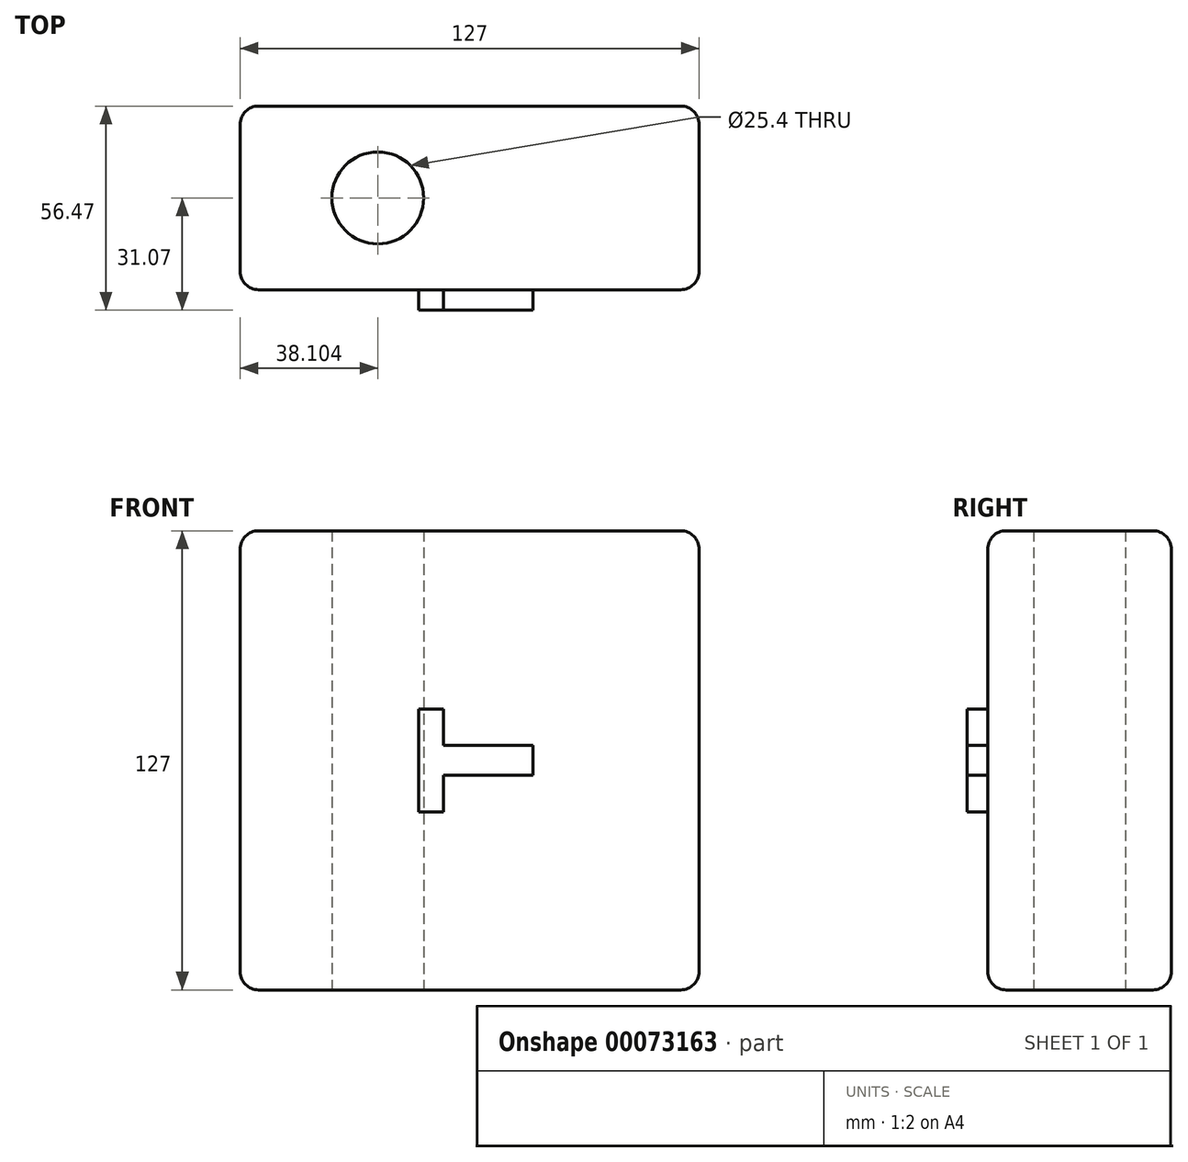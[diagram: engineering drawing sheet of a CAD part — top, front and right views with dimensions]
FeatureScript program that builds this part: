
annotation { "Feature Type Name" : "Feature", "Feature Type Description" : "" }
export const myFeature = defineFeature(function(context is Context, id is Id, definition is map)
    precondition{}
    {
        {
            var Q0;
            Q0=qCreatedBy(makeId("Front.planeOp"),FACE);
            var sketch = newSketch(context, id + "F0", { "sketchPlane" : qUnion([Q0])});
            skLineSegment(sketch, "E0.bottom", {"start": v(-63.03, 57.85) * mm, "end": v(63.97, 57.85) * mm});
            skLineSegment(sketch, "E0.top", {"start": v(-63.03, -69.15) * mm, "end": v(63.97, -69.15) * mm});
            skLineSegment(sketch, "E0.left", {"start": v(-63.03, 57.85) * mm, "end": v(-63.03, -69.15) * mm});
            skLineSegment(sketch, "E0.right", {"start": v(63.97, 57.85) * mm, "end": v(63.97, -69.15) * mm});
            skSolve(sketch);
        }
        {
            var Q0;
            Q0=makeQuery(id+"F0.imprint","IMPRINT",FACE,{"disambiguationData":[TD([[makeQuery(id+"F0.imprint","IMPRINT",EDGE,{"derivedFrom":sQuery(id+"F0.wireOp",EDGE,"E0.bottom")}),-1.0]])]});
            extrude(context, id + "F1", {"entities" : qUnion([Q0]), "depth" : 50.8 * mm});
        }
        {
            var Q0;
            Q0=makeQuery(id+"F1.opExtrude","CAP_EDGE",EDGE,{"disambiguationData":[OSD([sQuery(id+"F0.wireOp",EDGE,"E0.top")])],"isStart":false});
            var Q1;
            Q1=makeQuery(id+"F1.opExtrude","CAP_EDGE",EDGE,{"disambiguationData":[OSD([sQuery(id+"F0.wireOp",EDGE,"E0.top")])],"isStart":true});
            var Q2;
            Q2=makeQuery(id+"F1.opExtrude","CAP_EDGE",EDGE,{"disambiguationData":[OSD([sQuery(id+"F0.wireOp",EDGE,"E0.bottom")])],"isStart":true});
            var Q3;
            Q3=makeQuery(id+"F1.opExtrude","CAP_EDGE",EDGE,{"disambiguationData":[OSD([sQuery(id+"F0.wireOp",EDGE,"E0.bottom")])],"isStart":false});
            var Q4;
            Q4=makeQuery(id+"F1.opExtrude","CAP_EDGE",EDGE,{"disambiguationData":[OSD([sQuery(id+"F0.wireOp",EDGE,"E0.left")])],"isStart":false});
            var Q5;
            Q5=makeQuery(id+"F1.opExtrude","CAP_EDGE",EDGE,{"disambiguationData":[OSD([sQuery(id+"F0.wireOp",EDGE,"E0.left")])],"isStart":true});
            var Q6;
            Q6=makeQuery(id+"F1.opExtrude","SWEPT_FACE",FACE,{"disambiguationData":[OSD([sQuery(id+"F0.wireOp",EDGE,"E0.left")])]});
            var Q7;
            Q7=makeQuery(id+"F1.opExtrude","SWEPT_FACE",FACE,{"disambiguationData":[OSD([sQuery(id+"F0.wireOp",EDGE,"E0.right")])]});
            fillet(context, id + "F2", {"entities" : qUnion([Q0, Q1, Q2, Q3, Q4, Q5, Q6, Q7]), "radius" : 5.08 * mm, "tangentPropagation" : true, "allowEdgeOverflow" : false});
        }
        {
            var Q0;
            Q0=makeQuery(id+"F1.opExtrude","CAP_FACE",FACE,{"disambiguationData":[OSD([sQuery(id+"F0.wireOp",EDGE,"E0.bottom"),sQuery(id+"F0.wireOp",EDGE,"E0.top"),sQuery(id+"F0.wireOp",EDGE,"E0.left"),sQuery(id+"F0.wireOp",EDGE,"E0.right")])],"isStart":false});
            var sketch = newSketch(context, id + "F3", { "sketchPlane" : qUnion([Q0])});
            skLineSegment(sketch, "E1", {"start": v(-13.66, -19.88) * mm, "end": v(-6.77, -19.88) * mm});
            skLineSegment(sketch, "E2", {"start": v(-6.77, -19.88) * mm, "end": v(-6.77, -9.78) * mm});
            skLineSegment(sketch, "E3", {"start": v(-6.77, -9.78) * mm, "end": v(18.02, -9.78) * mm});
            skLineSegment(sketch, "E4", {"start": v(18.02, -9.78) * mm, "end": v(18.02, -1.52) * mm});
            skLineSegment(sketch, "E5", {"start": v(18.02, -1.52) * mm, "end": v(-6.77, -1.52) * mm});
            skLineSegment(sketch, "E6", {"start": v(-6.77, -1.52) * mm, "end": v(-6.77, 8.58) * mm});
            skLineSegment(sketch, "E7", {"start": v(-6.77, 8.58) * mm, "end": v(-13.66, 8.58) * mm});
            skLineSegment(sketch, "E8", {"start": v(-13.66, 8.58) * mm, "end": v(-13.66, -19.88) * mm});
            skPoint(sketch, "E9.startSnap0", {"position": v(-13.66, -5.65) * mm});
            skLineSegment(sketch, "E10", {"start": v(-57.95, -5.65) * mm, "end": v(-13.66, -5.65) * mm, "construction": true});
            skLineSegment(sketch, "E11", {"start": v(-13.66, -5.65) * mm, "end": v(-13.66, 52.77) * mm, "construction": true});
            skSolve(sketch);
        }
        {
            var Q0;
            Q0 = qSketchRegion(id + "F3", true);
            extrude(context, id + "F4", {"entities" : qUnion([Q0]), "operationType" : NewBodyOperationType.ADD, "depth" : 5.67 * mm});
        }
        {
            var Q0;
            Q0=makeQuery(id+"F1.opExtrude","SWEPT_FACE",FACE,{"disambiguationData":[OSD([sQuery(id+"F0.wireOp",EDGE,"E0.top")])]});
            var sketch = newSketch(context, id + "F5", { "sketchPlane" : qUnion([Q0])});
            skCircle(sketch, "E12", {"center": v(-24.93, 25.4) * mm, "radius": 12.7 * mm});
            skLineSegment(sketch, "E13", {"start": v(-57.95, 25.4) * mm, "end": v(-24.93, 25.4) * mm});
            skSolve(sketch);
        }
        {
            var Q0;
            Q0=makeQuery(id+"F5.imprint","IMPRINT",FACE,{"disambiguationData":[TD([[makeQuery(id+"F5.imprint","IMPRINT",EDGE,{"derivedFrom":sQuery(id+"F5.wireOp",EDGE,"E12")}),1.0]])]});
            var Q1;
            Q1 = qConstructionFilter(qBodyType(qCreatedBy(id + "F5" ,EDGE), BodyType.WIRE), ConstructionObject.NO);
            extrude(context, id + "F6", {"entities" : qUnion([Q0]), "operationType" : NewBodyOperationType.REMOVE, "surfaceEntities" : qUnion([Q1]), "endBound" : BoundingType.THROUGH_ALL, "oppositeDirection" : true, "depth" : 25.4 * mm});
        }
    });
